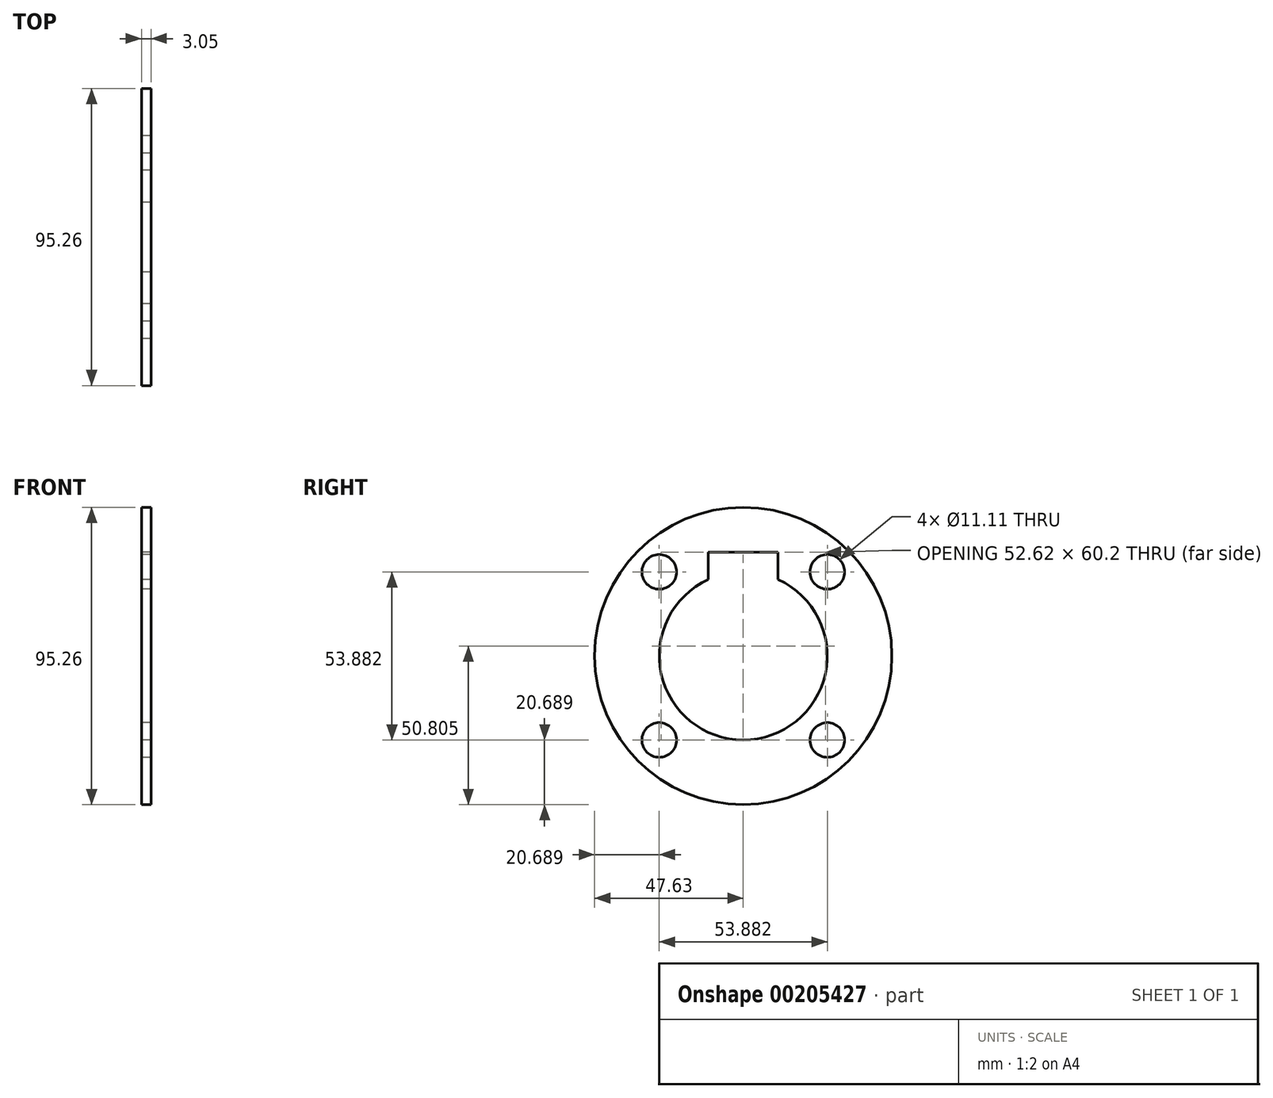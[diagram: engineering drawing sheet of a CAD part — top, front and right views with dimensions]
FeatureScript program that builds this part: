
annotation { "Feature Type Name" : "Feature", "Feature Type Description" : "" }
export const myFeature = defineFeature(function(context is Context, id is Id, definition is map)
    precondition{}
    {
        {
            var Q0;
            Q0=qCreatedBy(makeId("Right.planeOp"),FACE);
            var sketch = newSketch(context, id + "F0", { "sketchPlane" : qUnion([Q0])});
            skCircle(sketch, "E0", {"center": v(0, 0) * mm, "radius": 47.63 * mm});
            skArc(sketch, "E1", {"start": v(-11.18, 24.5) * mm, "mid": v(0, -26.92) * mm, "end": v(11.18, 24.5) * mm});
            skLineSegment(sketch, "E2", {"start": v(0, 0) * mm, "end": v(70.22, 0) * mm, "construction": true});
            skLineSegment(sketch, "E3", {"start": v(0, 0) * mm, "end": v(0, 59.17) * mm, "construction": true});
            skLineSegment(sketch, "E4.0", {"start": v(0, 33.27) * mm, "end": v(70.22, 33.27) * mm, "construction": true});
            skLineSegment(sketch, "E5.0", {"start": v(11.18, 0) * mm, "end": v(11.18, 20.57) * mm, "construction": true});
            skLineSegment(sketch, "E6.bottom", {"start": v(11.18, 33.27) * mm, "end": v(-11.18, 33.27) * mm});
            skLineSegment(sketch, "E6.left", {"start": v(11.18, 33.27) * mm, "end": v(11.18, 20.57) * mm});
            skLineSegment(sketch, "E6.right", {"start": v(-11.18, 33.27) * mm, "end": v(-11.18, 24.5) * mm});
            skLineSegment(sketch, "E7.trimOffspring", {"start": v(11.18, 24.5) * mm, "end": v(11.18, 59.17) * mm, "construction": true});
            skCircle(sketch, "E8", {"center": v(0, 0) * mm, "radius": 38.1 * mm, "construction": true});
            skLineSegment(sketch, "E9", {"start": v(0, 0) * mm, "end": v(-42.76, 42.76) * mm, "construction": true});
            skLineSegment(sketch, "E10", {"start": v(-42.76, 42.76) * mm, "end": v(-17.32, 57.62) * mm, "construction": true});
            skPoint(sketch, "E11", {"position": v(-26.94, 26.94) * mm});
            skPoint(sketch, "E12.1.0", {"position": v(-26.94, -26.94) * mm});
            skPoint(sketch, "E12.2.0", {"position": v(26.94, -26.94) * mm});
            skPoint(sketch, "E12.3.0", {"position": v(26.94, 26.94) * mm});
            skCircle(sketch, "E13", {"center": v(-26.94, 26.94) * mm, "radius": 5.56 * mm});
            skCircle(sketch, "E14", {"center": v(-26.94, -26.94) * mm, "radius": 5.56 * mm});
            skCircle(sketch, "E15", {"center": v(26.94, -26.94) * mm, "radius": 5.56 * mm});
            skCircle(sketch, "E16", {"center": v(26.94, 26.94) * mm, "radius": 5.56 * mm});
            skSolve(sketch);
        }
        {
            var Q0;
            Q0 = qSketchRegion(id + "F0", true);
            extrude(context, id + "F1", {"entities" : qUnion([Q0]), "depth" : 3.05 * mm});
        }
    });
